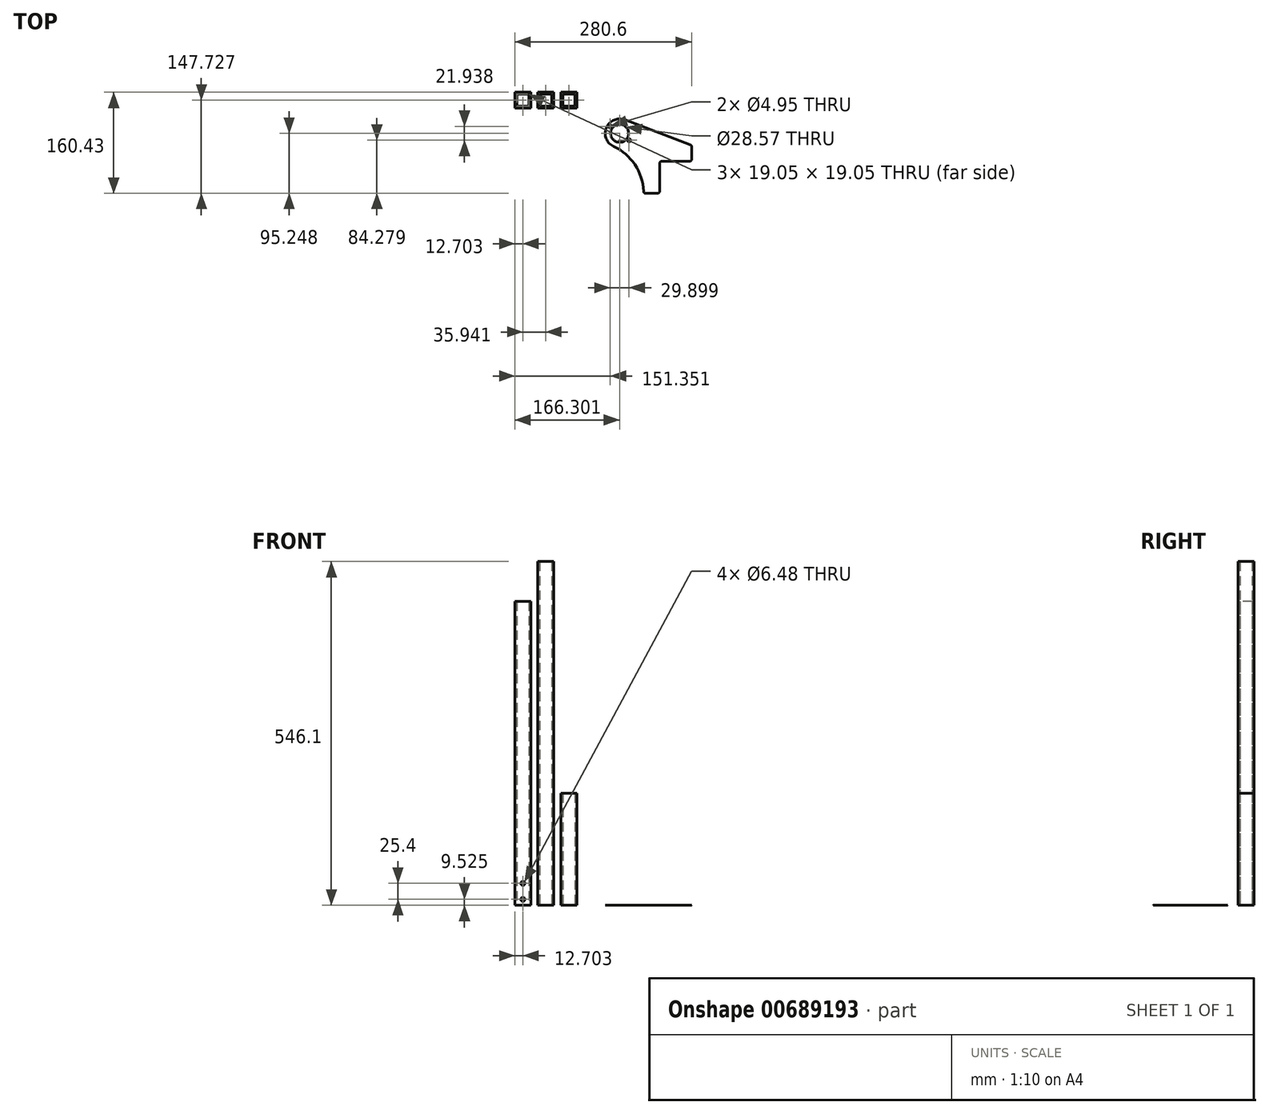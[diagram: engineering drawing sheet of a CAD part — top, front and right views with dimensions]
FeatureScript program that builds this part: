
annotation { "Feature Type Name" : "Feature", "Feature Type Description" : "" }
export const myFeature = defineFeature(function(context is Context, id is Id, definition is map)
    precondition{}
    {
        {
            var Q0;
            Q0=qCreatedBy(makeId("Top.planeOp"),FACE);
            var sketch = newSketch(context, id + "F0", { "sketchPlane" : qUnion([Q0])});
            skLineSegment(sketch, "E0.bottom", {"start": v(-84.43, 55.85) * mm, "end": v(-59.03, 55.85) * mm});
            skLineSegment(sketch, "E0.top", {"start": v(-84.43, 30.45) * mm, "end": v(-59.03, 30.45) * mm});
            skLineSegment(sketch, "E0.left", {"start": v(-84.43, 55.85) * mm, "end": v(-84.43, 30.45) * mm});
            skLineSegment(sketch, "E0.right", {"start": v(-59.03, 55.85) * mm, "end": v(-59.03, 30.45) * mm});
            skPoint(sketch, "E0.middle", {"position": v(-71.73, 43.15) * mm});
            skLineSegment(sketch, "E1.bottom", {"start": v(-81.25, 52.67) * mm, "end": v(-62.2, 52.67) * mm});
            skLineSegment(sketch, "E1.top", {"start": v(-81.25, 33.62) * mm, "end": v(-62.2, 33.62) * mm});
            skLineSegment(sketch, "E1.left", {"start": v(-81.25, 52.67) * mm, "end": v(-81.25, 33.62) * mm});
            skLineSegment(sketch, "E1.right", {"start": v(-62.2, 52.67) * mm, "end": v(-62.2, 33.62) * mm});
            skLineSegment(sketch, "E2.bottom", {"start": v(-23.09, 30.45) * mm, "end": v(-48.49, 30.45) * mm});
            skLineSegment(sketch, "E2.top", {"start": v(-23.09, 55.85) * mm, "end": v(-48.49, 55.85) * mm});
            skLineSegment(sketch, "E2.left", {"start": v(-23.09, 30.45) * mm, "end": v(-23.09, 55.85) * mm});
            skLineSegment(sketch, "E2.right", {"start": v(-48.49, 30.45) * mm, "end": v(-48.49, 55.85) * mm});
            skPoint(sketch, "E2.middle", {"position": v(-35.79, 43.15) * mm});
            skLineSegment(sketch, "E3.bottom", {"start": v(-26.26, 33.62) * mm, "end": v(-45.31, 33.62) * mm});
            skLineSegment(sketch, "E3.top", {"start": v(-26.26, 52.67) * mm, "end": v(-45.31, 52.67) * mm});
            skLineSegment(sketch, "E3.left", {"start": v(-26.26, 33.62) * mm, "end": v(-26.26, 52.67) * mm});
            skLineSegment(sketch, "E3.right", {"start": v(-45.31, 33.62) * mm, "end": v(-45.31, 52.67) * mm});
            skLineSegment(sketch, "E4.bottom", {"start": v(13.83, 30.45) * mm, "end": v(-11.57, 30.45) * mm});
            skLineSegment(sketch, "E4.top", {"start": v(13.83, 55.85) * mm, "end": v(-11.57, 55.85) * mm});
            skLineSegment(sketch, "E4.left", {"start": v(13.83, 30.45) * mm, "end": v(13.83, 55.85) * mm});
            skLineSegment(sketch, "E4.right", {"start": v(-11.57, 30.45) * mm, "end": v(-11.57, 55.85) * mm});
            skPoint(sketch, "E4.middle", {"position": v(1.13, 43.15) * mm});
            skLineSegment(sketch, "E5.bottom", {"start": v(10.66, 33.62) * mm, "end": v(-8.4, 33.62) * mm});
            skLineSegment(sketch, "E5.top", {"start": v(10.66, 52.67) * mm, "end": v(-8.4, 52.67) * mm});
            skLineSegment(sketch, "E5.left", {"start": v(10.66, 33.62) * mm, "end": v(10.66, 52.67) * mm});
            skLineSegment(sketch, "E5.right", {"start": v(-8.4, 33.62) * mm, "end": v(-8.4, 52.67) * mm});
            skSolve(sketch);
        }
        {
            var Q0;
            Q0=makeQuery(id+"F0.imprint","IMPRINT",FACE,{"disambiguationData":[TD([[makeQuery(id+"F0.imprint","IMPRINT",EDGE,{"derivedFrom":sQuery(id+"F0.wireOp",EDGE,"E0.bottom")}),-1.0]])]});
            extrude(context, id + "F1", {"entities" : qUnion([Q0]), "depth" : 482.6 * mm, "offsetDistance" : 25.4 * mm});
        }
        {
            var Q0;
            Q0=makeQuery(id+"F1.opExtrude","SWEPT_FACE",FACE,{"disambiguationData":[OSD([sQuery(id+"F0.wireOp",EDGE,"E0.top")])]});
            var sketch = newSketch(context, id + "F2", { "sketchPlane" : qUnion([Q0])});
            skLineSegment(sketch, "E6.0.0", {"start": v(-84.43, 0) * mm, "end": v(-59.03, 0) * mm, "construction": true});
            skLineSegment(sketch, "E6.0.1", {"start": v(-59.03, 0) * mm, "end": v(-59.03, 482.6) * mm, "construction": true});
            skLineSegment(sketch, "E6.0.2", {"start": v(-59.03, 482.6) * mm, "end": v(-84.43, 482.6) * mm, "construction": true});
            skLineSegment(sketch, "E6.0.3", {"start": v(-84.43, 482.6) * mm, "end": v(-84.43, 0) * mm, "construction": true});
            skCircle(sketch, "E7", {"center": v(-71.73, 9.53) * mm, "radius": 3.24 * mm});
            skPoint(sketch, "E7.centerSnap0", {"position": v(-71.73, 0) * mm});
            skCircle(sketch, "E8", {"center": v(-71.73, 34.92) * mm, "radius": 3.24 * mm});
            skSolve(sketch);
        }
        {
            var Q0;
            Q0=makeQuery(id+"F2.imprint","IMPRINT",FACE,{"disambiguationData":[TD([[makeQuery(id+"F2.imprint","IMPRINT",EDGE,{"derivedFrom":sQuery(id+"F2.wireOp",EDGE,"E8")}),1.0]])]});
            var Q1;
            Q1=makeQuery(id+"F2.imprint","IMPRINT",FACE,{"disambiguationData":[TD([[makeQuery(id+"F2.imprint","IMPRINT",EDGE,{"derivedFrom":sQuery(id+"F2.wireOp",EDGE,"E7")}),1.0]])]});
            var Q2;
            Q2=makeQuery(id+"F1.opExtrude","SWEPT_FACE",FACE,{"disambiguationData":[OSD([sQuery(id+"F0.wireOp",EDGE,"E0.bottom")])]});
            extrude(context, id + "F3", {"entities" : qUnion([Q0, Q1]), "operationType" : NewBodyOperationType.REMOVE, "endBound" : BoundingType.UP_TO_SURFACE, "oppositeDirection" : true, "depth" : 25.4 * mm, "endBoundEntityFace" : qUnion([Q2]), "offsetDistance" : 25.4 * mm});
        }
        {
            var Q0;
            Q0=makeQuery(id+"F0.imprint","IMPRINT",FACE,{"disambiguationData":[TD([[makeQuery(id+"F0.imprint","IMPRINT",EDGE,{"derivedFrom":sQuery(id+"F0.wireOp",EDGE,"E2.bottom")}),-1.0]])]});
            extrude(context, id + "F4", {"entities" : qUnion([Q0]), "depth" : 546.1 * mm, "offsetDistance" : 25.4 * mm});
        }
        {
            var Q0;
            Q0=makeQuery(id+"F0.imprint","IMPRINT",FACE,{"disambiguationData":[TD([[makeQuery(id+"F0.imprint","IMPRINT",EDGE,{"derivedFrom":sQuery(id+"F0.wireOp",EDGE,"E4.bottom")}),-1.0]])]});
            extrude(context, id + "F5", {"entities" : qUnion([Q0]), "depth" : 177.8 * mm, "offsetDistance" : 25.4 * mm});
        }
        {
            var Q0;
            Q0=qCreatedBy(makeId("Top.planeOp"),FACE);
            var sketch = newSketch(context, id + "F6", { "sketchPlane" : qUnion([Q0])});
            skCircle(sketch, "E9", {"center": v(81.87, -9.33) * mm, "radius": 14.29 * mm});
            skCircle(sketch, "E10", {"center": v(81.87, -9.33) * mm, "radius": 15.56 * mm, "construction": true});
            skArc(sketch, "E11", {"start": v(90, 12.03) * mm, "mid": v(60.8, -0.47) * mm, "end": v(72.3, -30.1) * mm});
            skLineSegment(sketch, "E12", {"start": v(196.17, -53.78) * mm, "end": v(145.37, -53.78) * mm});
            skLineSegment(sketch, "E13", {"start": v(145.37, -53.78) * mm, "end": v(145.37, -104.58) * mm});
            skLineSegment(sketch, "E14", {"start": v(145.37, -104.58) * mm, "end": v(119.97, -104.58) * mm});
            skLineSegment(sketch, "E15", {"start": v(196.17, -53.78) * mm, "end": v(196.17, -28.38) * mm});
            skLineSegment(sketch, "E16", {"start": v(196.17, -28.38) * mm, "end": v(90, 12.03) * mm});
            skArc(sketch, "E17", {"start": v(119.97, -104.58) * mm, "mid": v(107.03, -60.36) * mm, "end": v(72.3, -30.1) * mm});
            skLineSegment(sketch, "E18", {"start": v(119.97, -104.58) * mm, "end": v(119.97, -28.38) * mm, "construction": true});
            skLineSegment(sketch, "E19", {"start": v(119.97, -28.38) * mm, "end": v(196.17, -28.38) * mm, "construction": true});
            skCircle(sketch, "E20", {"center": v(66.92, 1.64) * mm, "radius": 2.48 * mm});
            skCircle(sketch, "E21", {"center": v(96.82, -20.3) * mm, "radius": 2.48 * mm});
            skLineSegment(sketch, "E22", {"start": v(96.82, -20.3) * mm, "end": v(66.92, 1.64) * mm, "construction": true});
            skLineSegment(sketch, "E23.bottom", {"start": v(145.37, -53.78) * mm, "end": v(196.17, -53.78) * mm});
            skCircle(sketch, "E24", {"center": v(170.73, -79.18) * mm, "radius": 9.53 * mm});
            skCircle(sketch, "E25", {"center": v(170.73, -79.18) * mm, "radius": 25.4 * mm, "construction": true});
            skLineSegment(sketch, "E26", {"start": v(188.7, -97.14) * mm, "end": v(152.77, -61.22) * mm, "construction": true});
            skCircle(sketch, "E27", {"center": v(152.77, -61.22) * mm, "radius": 2.55 * mm});
            skCircle(sketch, "E28", {"center": v(188.7, -97.14) * mm, "radius": 2.55 * mm});
            skLineSegment(sketch, "E29", {"start": v(196.17, -53.78) * mm, "end": v(201.72, -53.78) * mm});
            skLineSegment(sketch, "E30", {"start": v(201.72, -53.78) * mm, "end": v(201.72, -104.58) * mm});
            skLineSegment(sketch, "E31", {"start": v(201.72, -104.58) * mm, "end": v(145.37, -104.58) * mm});
            skSolve(sketch);
        }
        {
            var Q0;
            Q0=makeQuery(id+"F6.imprint","IMPRINT",FACE,{"disambiguationData":[TD([[makeQuery(id+"F6.imprint","IMPRINT",EDGE,{"derivedFrom":sQuery(id+"F6.wireOp",EDGE,"E9")}),-1.0]])]});
            var Q1;
            Q1=makeQuery(id+"F6.imprint","IMPRINT",FACE,{"disambiguationData":[TD([[makeQuery(id+"F6.imprint","IMPRINT",EDGE,{"derivedFrom":sQuery(id+"F6.wireOp",EDGE,"E23.bottom")}),-1.0]])]});
            extrude(context, id + "F7", {"entities" : qUnion([Q0, Q1]), "depth" : 1 / 101.6 * mm, "offsetDistance" : 25.4 * mm});
        }
        {
            var Q0;
            Q0=makeQuery(id+"F7.opExtrude","SWEPT_EDGE",EDGE,{"disambiguationData":[OSD([sQuery(id+"F6.wireOp",EDGE,"E15"),sQuery(id+"F6.wireOp",EDGE,"E16")])]});
            var Q1;
            Q1=makeQuery(id+"F7.opExtrude","SWEPT_EDGE",EDGE,{"disambiguationData":[OSD([sQuery(id+"F6.wireOp",EDGE,"E12"),sQuery(id+"F6.wireOp",EDGE,"E15")])]});
            var Q2;
            Q2=makeQuery(id+"F7.opExtrude","SWEPT_EDGE",EDGE,{"disambiguationData":[OSD([sQuery(id+"F6.wireOp",EDGE,"E12"),sQuery(id+"F6.wireOp",EDGE,"E13")])]});
            var Q3;
            Q3=makeQuery(id+"F7.opExtrude","SWEPT_EDGE",EDGE,{"disambiguationData":[OSD([sQuery(id+"F6.wireOp",EDGE,"E13"),sQuery(id+"F6.wireOp",EDGE,"E14")])]});
            var Q4;
            Q4=makeQuery(id+"F7.opExtrude","SWEPT_EDGE",EDGE,{"disambiguationData":[OSD([sQuery(id+"F6.wireOp",EDGE,"E14"),sQuery(id+"F6.wireOp",EDGE,"E17")])]});
            var Q5;
            Q5=makeQuery(id+"F7.opExtrude","SWEPT_EDGE",EDGE,{"disambiguationData":[OSD([sQuery(id+"F6.wireOp",EDGE,"E29"),sQuery(id+"F6.wireOp",EDGE,"E30")])]});
            var Q6;
            Q6=makeQuery(id+"F7.opExtrude","SWEPT_EDGE",EDGE,{"disambiguationData":[OSD([sQuery(id+"F6.wireOp",EDGE,"E30"),sQuery(id+"F6.wireOp",EDGE,"E31")])]});
            fillet(context, id + "F8", {"entities" : qUnion([Q0, Q1, Q2, Q3, Q4, Q5, Q6]), "radius" : 3.17 * mm, "tangentPropagation" : true, "allowEdgeOverflow" : false});
        }
    });
